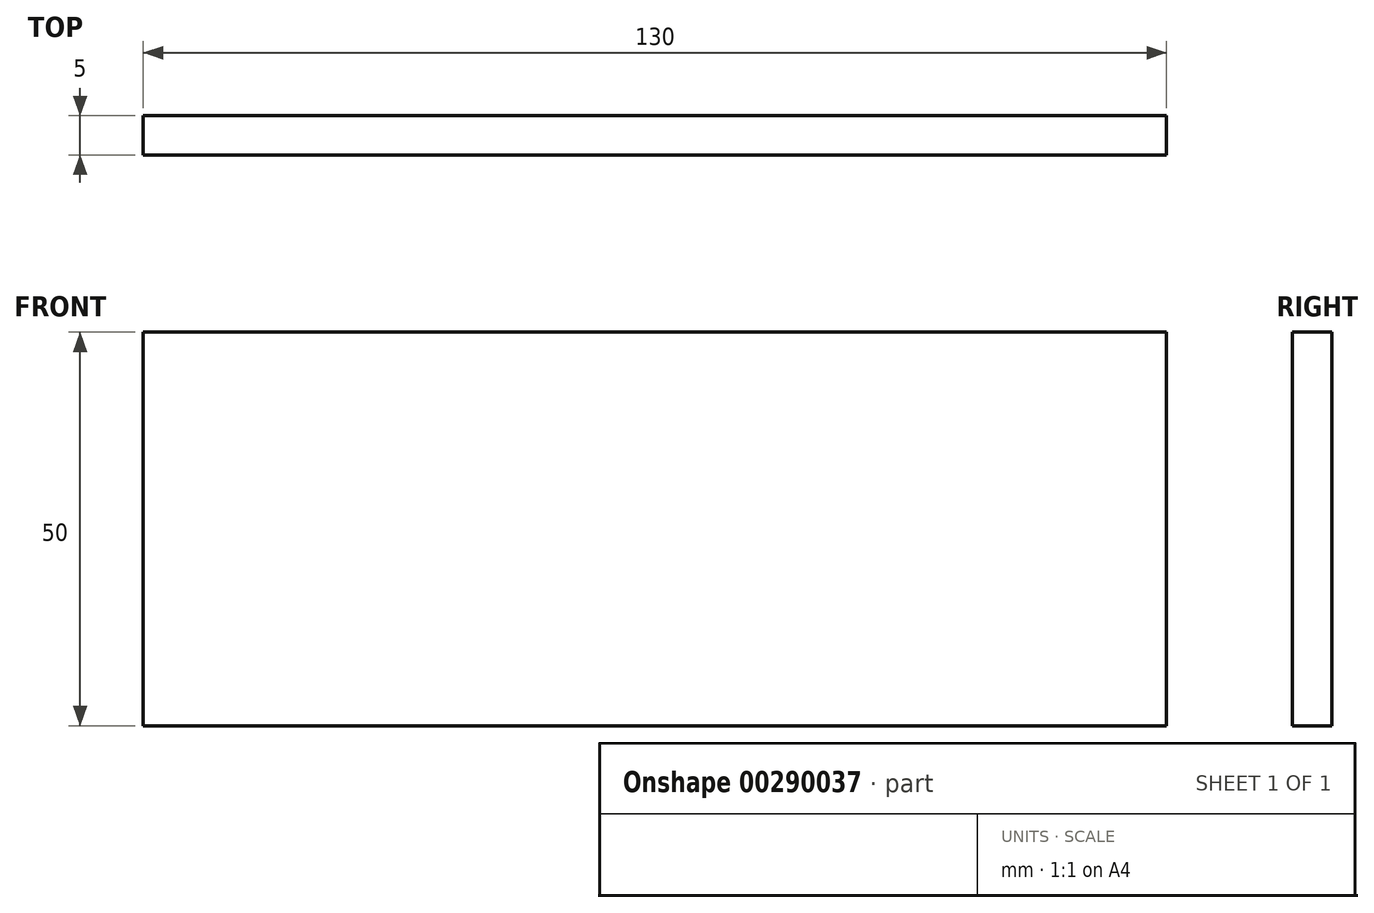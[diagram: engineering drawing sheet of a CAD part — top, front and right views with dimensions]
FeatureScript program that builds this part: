
annotation { "Feature Type Name" : "Feature", "Feature Type Description" : "" }
export const myFeature = defineFeature(function(context is Context, id is Id, definition is map)
    precondition{}
    {
        {
            var Q0;
            Q0=qCreatedBy(makeId("Front.planeOp"),FACE);
            var sketch = newSketch(context, id + "F0", { "sketchPlane" : qUnion([Q0])});
            skLineSegment(sketch, "E0.bottom", {"start": v(-50.52, 44.63) * mm, "end": v(79.48, 44.63) * mm});
            skLineSegment(sketch, "E0.top", {"start": v(-50.52, -5.37) * mm, "end": v(79.48, -5.37) * mm});
            skLineSegment(sketch, "E0.left", {"start": v(-50.52, 44.63) * mm, "end": v(-50.52, -5.37) * mm});
            skLineSegment(sketch, "E0.right", {"start": v(79.48, 44.63) * mm, "end": v(79.48, -5.37) * mm});
            skSolve(sketch);
        }
        {
            var Q0;
            Q0 = qSketchRegion(id + "F0", true);
            extrude(context, id + "F1", {"entities" : qUnion([Q0]), "depth" : 5 * mm});
        }
    });
